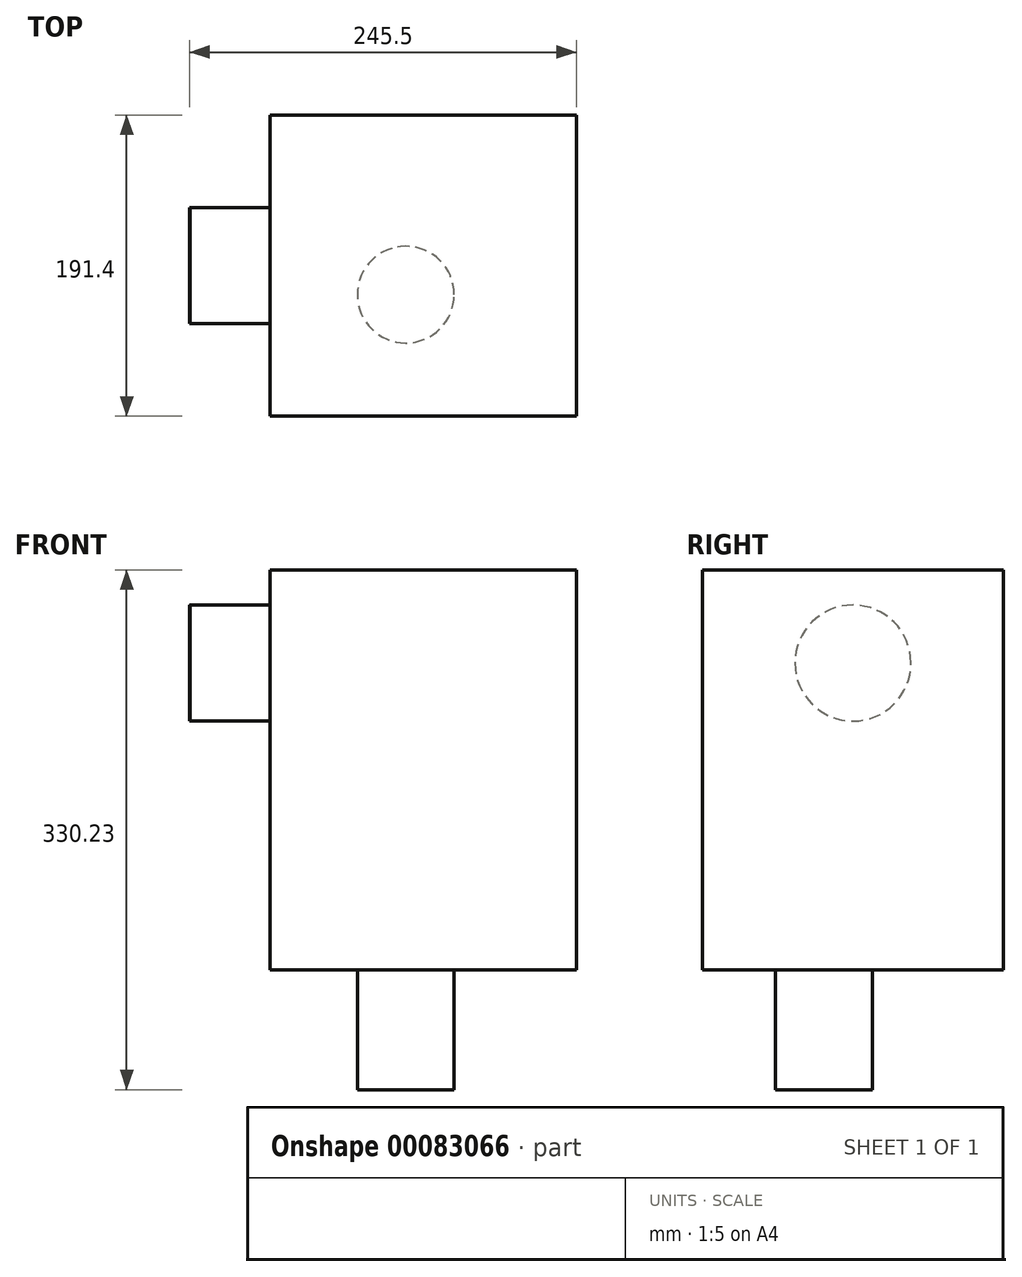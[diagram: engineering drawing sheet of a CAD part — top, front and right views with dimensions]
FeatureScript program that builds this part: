
annotation { "Feature Type Name" : "Feature", "Feature Type Description" : "" }
export const myFeature = defineFeature(function(context is Context, id is Id, definition is map)
    precondition{}
    {
        {
            var Q0;
            Q0=qCreatedBy(makeId("Top.planeOp"),FACE);
            var sketch = newSketch(context, id + "F0", { "sketchPlane" : qUnion([Q0])});
            skLineSegment(sketch, "E0.bottom", {"start": v(-97.34, 95.7) * mm, "end": v(97.34, 95.7) * mm});
            skLineSegment(sketch, "E0.top", {"start": v(-97.34, -95.7) * mm, "end": v(97.34, -95.7) * mm});
            skLineSegment(sketch, "E0.left", {"start": v(-97.34, 95.7) * mm, "end": v(-97.34, -95.7) * mm});
            skLineSegment(sketch, "E0.right", {"start": v(97.34, 95.7) * mm, "end": v(97.34, -95.7) * mm});
            skPoint(sketch, "E0.middle", {"position": v(0, 0) * mm});
            skSolve(sketch);
        }
        {
            var Q0;
            Q0=makeQuery(id+"F0.imprint","IMPRINT",FACE,{"disambiguationData":[TD([[makeQuery(id+"F0.imprint","IMPRINT",EDGE,{"derivedFrom":sQuery(id+"F0.wireOp",EDGE,"E0.bottom")}),-1.0]])]});
            var Q1;
            Q1=sQuery(id+"F0.wireOp",EDGE,"E0.left");
            var Q2;
            Q2=sQuery(id+"F0.wireOp",EDGE,"E0.top");
            var Q3;
            Q3=sQuery(id+"F0.wireOp",EDGE,"E0.right");
            var Q4;
            Q4=sQuery(id+"F0.wireOp",EDGE,"E0.bottom");
            extrude(context, id + "F1", {"entities" : qUnion([Q0]), "surfaceEntities" : qUnion([Q1, Q2, Q3, Q4]), "endBound" : BoundingType.SYMMETRIC, "depth" : 254 * mm});
        }
        {
            var Q0;
            Q0=makeQuery(id+"F1.opExtrude","SWEPT_FACE",FACE,{"disambiguationData":[OSD([sQuery(id+"F0.wireOp",EDGE,"E0.left")])]});
            var sketch = newSketch(context, id + "F2", { "sketchPlane" : qUnion([Q0])});
            skCircle(sketch, "E1", {"center": v(0, 67.73) * mm, "radius": 36.83 * mm});
            skSolve(sketch);
        }
        {
            var Q0;
            Q0 = qSketchRegion(id + "F2", true);
            var Q1;
            Q1=sQuery(id+"F2.wireOp",EDGE,"E1");
            extrude(context, id + "F3", {"entities" : qUnion([Q0]), "operationType" : NewBodyOperationType.ADD, "surfaceEntities" : qUnion([Q1]), "depth" : 50.8 * mm});
        }
        {
            var Q0;
            Q0=makeQuery(id+"F1.opExtrude","CAP_FACE",FACE,{"disambiguationData":[OSD([sQuery(id+"F0.wireOp",EDGE,"E0.bottom"),sQuery(id+"F0.wireOp",EDGE,"E0.top"),sQuery(id+"F0.wireOp",EDGE,"E0.left"),sQuery(id+"F0.wireOp",EDGE,"E0.right")])],"isStart":true});
            var sketch = newSketch(context, id + "F4", { "sketchPlane" : qUnion([Q0])});
            skCircle(sketch, "E2", {"center": v(-11, 18.42) * mm, "radius": 30.74 * mm});
            skSolve(sketch);
        }
        {
            var Q0;
            Q0 = qSketchRegion(id + "F4", true);
            var Q1;
            Q1=sQuery(id+"F4.wireOp",EDGE,"E2");
            extrude(context, id + "F5", {"entities" : qUnion([Q0]), "operationType" : NewBodyOperationType.ADD, "surfaceEntities" : qUnion([Q1]), "depth" : 76.2 * mm});
        }
        {
            var Q0;
            Q0=makeQuery(id+"F3.opExtrude","CAP_FACE",FACE,{"disambiguationData":[OSD([sQuery(id+"F2.wireOp",EDGE,"E1")])],"isStart":false});
            extrude(context, id + "F6", {"entities" : qUnion([Q0]), "depth" : 0.03 * mm});
        }
        {
            var Q0;
            Q0=makeQuery(id+"F5.opExtrude","CAP_FACE",FACE,{"disambiguationData":[OSD([sQuery(id+"F4.wireOp",EDGE,"E2")])],"isStart":false});
            extrude(context, id + "F7", {"entities" : qUnion([Q0]), "depth" : 0.03 * mm});
        }
    });
